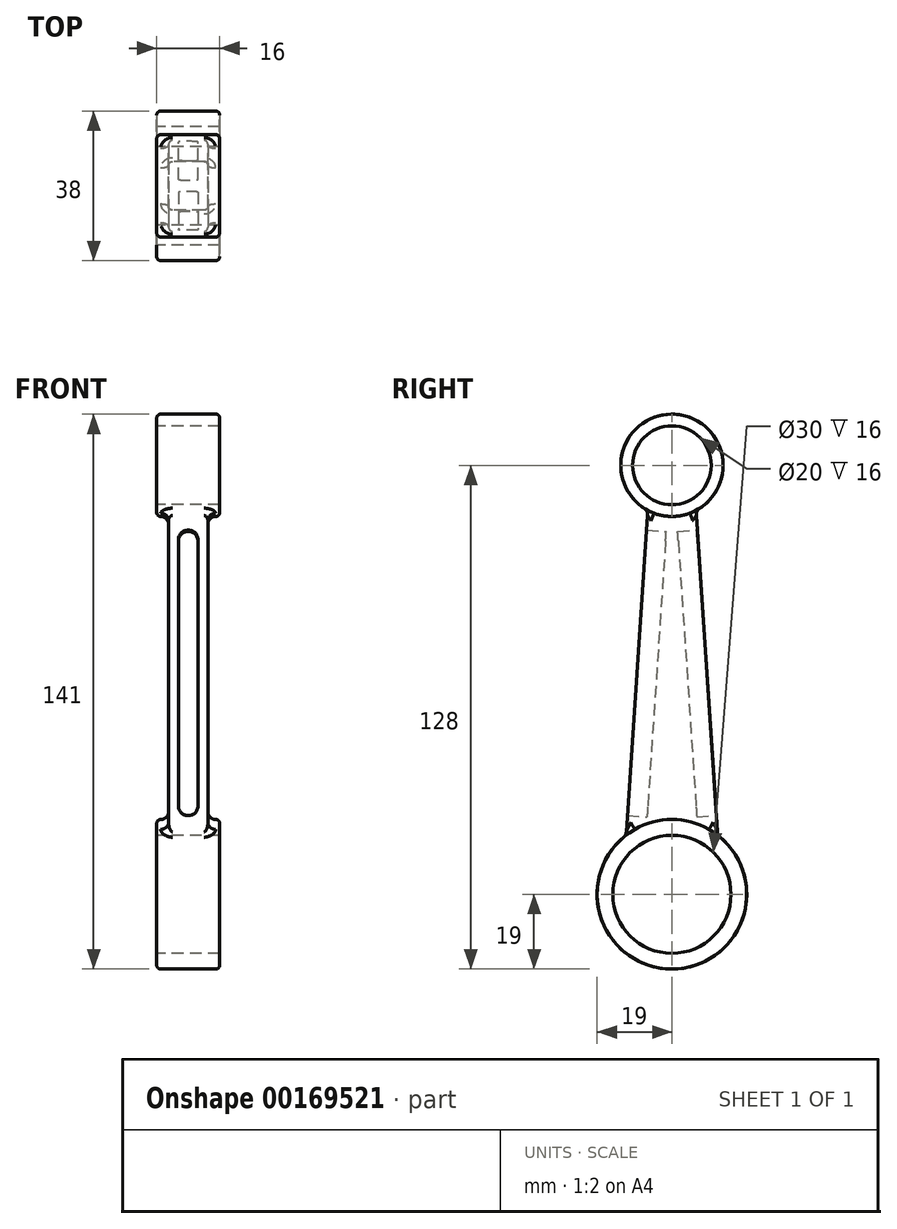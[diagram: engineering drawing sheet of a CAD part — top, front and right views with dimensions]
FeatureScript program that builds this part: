
annotation { "Feature Type Name" : "Feature", "Feature Type Description" : "" }
export const myFeature = defineFeature(function(context is Context, id is Id, definition is map)
    precondition{}
    {
        {
            assignVariable(context, id + "F0", {"name" : "BearingWidth", "anyValue" : 16});
        }
        {
            assignVariable(context, id + "F1", {"name" : "RodWidth", "anyValue" : 10});
        }
        {
            var Q0;
            Q0=qCreatedBy(makeId("Right.planeOp"),FACE);
            var sketch = newSketch(context, id + "F2", { "sketchPlane" : qUnion([Q0])});
            skCircle(sketch, "E0", {"center": v(0, 0) * mm, "radius": 19 * mm});
            skLineSegment(sketch, "E1", {"start": v(0, -34.78) * mm, "end": v(0, 151.53) * mm, "construction": true});
            skCircle(sketch, "E2", {"center": v(0, 109) * mm, "radius": 13 * mm});
            skCircle(sketch, "E3", {"center": v(0, 0) * mm, "radius": 15 * mm});
            skCircle(sketch, "E4", {"center": v(0, 109) * mm, "radius": 10 * mm});
            skSolve(sketch);
        }
        {
            var Q0;
            Q0 = qSketchRegion(id + "F2", true);
            extrude(context, id + "F3", {"entities" : qUnion([Q0]), "endBound" : BoundingType.SYMMETRIC, "depth" : (getVariable(context, 'BearingWidth')) * mm});
        }
        {
            var Q0;
            Q0=qCreatedBy(makeId("Right.planeOp"),FACE);
            var sketch = newSketch(context, id + "F4", { "sketchPlane" : qUnion([Q0])});
            skLineSegment(sketch, "E5", {"start": v(0, 136.56) * mm, "end": v(0, -23.65) * mm, "construction": true});
            skLineSegment(sketch, "E6", {"start": v(6, 99) * mm, "end": v(-6, 99) * mm});
            skCircle(sketch, "E7.0", {"center": v(0, 109) * mm, "radius": 10 * mm});
            skPoint(sketch, "E8", {"position": v(0, 99) * mm});
            skCircle(sketch, "E9.0", {"center": v(0, 0) * mm, "radius": 15 * mm});
            skPoint(sketch, "E10", {"position": v(0, 16.05) * mm});
            skLineSegment(sketch, "E11", {"start": v(0, 16.05) * mm, "end": v(-12, 9.7) * mm});
            skLineSegment(sketch, "E12", {"start": v(0, 16.05) * mm, "end": v(12, 9.7) * mm});
            skLineSegment(sketch, "E13", {"start": v(-6, 99) * mm, "end": v(-12, 9.7) * mm});
            skLineSegment(sketch, "E14", {"start": v(6, 99) * mm, "end": v(12, 9.7) * mm});
            skSolve(sketch);
        }
        {
            var Q0;
            Q0=makeQuery(id+"F4.imprint","IMPRINT",FACE,{"disambiguationData":[TD([[makeQuery(id+"F4.imprint","IMPRINT",EDGE,{"derivedFrom":sQuery(id+"F4.wireOp",EDGE,"E11")}),-1.0]])]});
            extrude(context, id + "F5", {"entities" : qUnion([Q0]), "operationType" : NewBodyOperationType.ADD, "endBound" : BoundingType.SYMMETRIC, "depth" : (getVariable(context, 'RodWidth')) * mm});
        }
        {
            var Q0;
            Q0=makeQuery(id+"F5.opExtrude","CAP_EDGE",EDGE,{"disambiguationData":[OSD([sQuery(id+"F4.wireOp",EDGE,"E13")])],"isStart":false});
            var Q1;
            Q1=makeQuery(id+"F3.opExtrude","CAP_EDGE",EDGE,{"disambiguationData":[OSD([sQuery(id+"F2.wireOp",EDGE,"E0")])],"isStart":false});
            var Q2;
            Q2=makeQuery(id+"F5.opExtrude","CAP_EDGE",EDGE,{"disambiguationData":[OSD([sQuery(id+"F4.wireOp",EDGE,"E14")])],"isStart":false});
            var Q3;
            Q3=makeQuery(id+"F3.opExtrude","CAP_EDGE",EDGE,{"disambiguationData":[OSD([sQuery(id+"F2.wireOp",EDGE,"E2")])],"isStart":false});
            var Q4;
            Q4=makeQuery(id+"F3.opExtrude","CAP_EDGE",EDGE,{"disambiguationData":[OSD([sQuery(id+"F2.wireOp",EDGE,"E0")])],"isStart":true});
            var Q5;
            Q5=makeQuery(id+"F5.opExtrude","CAP_EDGE",EDGE,{"disambiguationData":[OSD([sQuery(id+"F4.wireOp",EDGE,"E14")])],"isStart":true});
            var Q6;
            Q6=makeQuery(id+"F5.opExtrude","CAP_EDGE",EDGE,{"disambiguationData":[OSD([sQuery(id+"F4.wireOp",EDGE,"E13")])],"isStart":true});
            var Q7;
            Q7=makeQuery(id+"F3.opExtrude","CAP_EDGE",EDGE,{"disambiguationData":[OSD([sQuery(id+"F2.wireOp",EDGE,"E2")])],"isStart":true});
            fillet(context, id + "F6", {"entities" : qUnion([Q0, Q1, Q2, Q3, Q4, Q5, Q6, Q7]), "radius" : 1 * mm, "tangentPropagation" : true, "allowEdgeOverflow" : false});
        }
        {
            var Q0;
            Q0=makeQuery(id+"F5.opExtrude","SWEPT_FACE",FACE,{"disambiguationData":[OSD([sQuery(id+"F4.wireOp",EDGE,"E14")])]});
            var sketch = newSketch(context, id + "F7", { "sketchPlane" : qUnion([Q0])});
            skLineSegment(sketch, "E15", {"start": v(0, -3.9) * mm, "end": v(0, 157.82) * mm, "construction": true});
            skLineSegment(sketch, "E16.bottom", {"start": v(-2.5, 91.9) * mm, "end": v(2.5, 91.9) * mm});
            skLineSegment(sketch, "E16.top", {"start": v(-2.5, 19.2) * mm, "end": v(2.5, 19.2) * mm});
            skLineSegment(sketch, "E16.left", {"start": v(-2.5, 91.9) * mm, "end": v(-2.5, 19.2) * mm});
            skLineSegment(sketch, "E16.right", {"start": v(2.5, 91.9) * mm, "end": v(2.5, 19.2) * mm});
            skSolve(sketch);
        }
        {
            var Q0;
            Q0 = qSketchRegion(id + "F7", true);
            extrude(context, id + "F8", {"entities" : qUnion([Q0]), "operationType" : NewBodyOperationType.REMOVE, "oppositeDirection" : true, "depth" : 5 * mm});
        }
        {
            var Q0;
            Q0=makeQuery(id+"F8.boolean.opBoolean","COPY",EDGE,{"derivedFrom":makeQuery(id+"F8.opExtrude","SWEPT_EDGE",EDGE,{"disambiguationData":[OSD([sQuery(id+"F7.wireOp",EDGE,"E16.bottom"),sQuery(id+"F7.wireOp",EDGE,"E16.left")])]})});
            var Q1;
            Q1=makeQuery(id+"F8.boolean.opBoolean","COPY",EDGE,{"derivedFrom":makeQuery(id+"F8.opExtrude","SWEPT_EDGE",EDGE,{"disambiguationData":[OSD([sQuery(id+"F7.wireOp",EDGE,"E16.bottom"),sQuery(id+"F7.wireOp",EDGE,"E16.right")])]})});
            var Q2;
            Q2=makeQuery(id+"F8.boolean.opBoolean","COPY",EDGE,{"derivedFrom":makeQuery(id+"F8.opExtrude","SWEPT_EDGE",EDGE,{"disambiguationData":[OSD([sQuery(id+"F7.wireOp",EDGE,"E16.top"),sQuery(id+"F7.wireOp",EDGE,"E16.right")])]})});
            var Q3;
            Q3=makeQuery(id+"F8.boolean.opBoolean","COPY",EDGE,{"derivedFrom":makeQuery(id+"F8.opExtrude","SWEPT_EDGE",EDGE,{"disambiguationData":[OSD([sQuery(id+"F7.wireOp",EDGE,"E16.top"),sQuery(id+"F7.wireOp",EDGE,"E16.left")])]})});
            fillet(context, id + "F9", {"entities" : qUnion([Q0, Q1, Q2, Q3]), "radius" : 2.5 * mm, "tangentPropagation" : true, "allowEdgeOverflow" : false});
        }
        {
            var Q0;
            Q0=makeQuery(id+"F5.opExtrude","SWEPT_FACE",FACE,{"disambiguationData":[OSD([sQuery(id+"F4.wireOp",EDGE,"E13")])]});
            var sketch = newSketch(context, id + "F10", { "sketchPlane" : qUnion([Q0])});
            skLineSegment(sketch, "E17", {"start": v(0, 0) * mm, "end": v(0, 109.28) * mm, "construction": true});
            skPoint(sketch, "E17.endSnap0", {"position": v(0, 96.9) * mm});
            skLineSegment(sketch, "E18.bottom", {"start": v(-2.5, 91.9) * mm, "end": v(2.5, 91.9) * mm});
            skLineSegment(sketch, "E18.top", {"start": v(-2.5, 19.2) * mm, "end": v(2.5, 19.2) * mm});
            skLineSegment(sketch, "E18.left", {"start": v(-2.5, 91.9) * mm, "end": v(-2.5, 19.2) * mm});
            skLineSegment(sketch, "E18.right", {"start": v(2.5, 91.9) * mm, "end": v(2.5, 19.2) * mm});
            skSolve(sketch);
        }
        {
            var Q0;
            Q0 = qSketchRegion(id + "F10", true);
            extrude(context, id + "F11", {"entities" : qUnion([Q0]), "operationType" : NewBodyOperationType.REMOVE, "oppositeDirection" : true, "depth" : 5 * mm});
        }
        {
            var Q0;
            Q0=makeQuery(id+"F11.boolean.opBoolean","COPY",EDGE,{"derivedFrom":makeQuery(id+"F11.opExtrude","SWEPT_EDGE",EDGE,{"disambiguationData":[OSD([sQuery(id+"F10.wireOp",EDGE,"E18.bottom"),sQuery(id+"F10.wireOp",EDGE,"E18.right")])]})});
            var Q1;
            Q1=makeQuery(id+"F11.boolean.opBoolean","COPY",EDGE,{"derivedFrom":makeQuery(id+"F11.opExtrude","SWEPT_EDGE",EDGE,{"disambiguationData":[OSD([sQuery(id+"F10.wireOp",EDGE,"E18.bottom"),sQuery(id+"F10.wireOp",EDGE,"E18.left")])]})});
            var Q2;
            Q2=makeQuery(id+"F11.boolean.opBoolean","COPY",EDGE,{"derivedFrom":makeQuery(id+"F11.opExtrude","SWEPT_EDGE",EDGE,{"disambiguationData":[OSD([sQuery(id+"F10.wireOp",EDGE,"E18.top"),sQuery(id+"F10.wireOp",EDGE,"E18.left")])]})});
            var Q3;
            Q3=makeQuery(id+"F11.boolean.opBoolean","COPY",EDGE,{"derivedFrom":makeQuery(id+"F11.opExtrude","SWEPT_EDGE",EDGE,{"disambiguationData":[OSD([sQuery(id+"F10.wireOp",EDGE,"E18.top"),sQuery(id+"F10.wireOp",EDGE,"E18.right")])]})});
            fillet(context, id + "F12", {"entities" : qUnion([Q0, Q1, Q2, Q3]), "radius" : 2.5 * mm, "tangentPropagation" : true, "allowEdgeOverflow" : false});
        }
        {
            var Q0;
            Q0=makeQuery(id+"F5.boolean.opBoolean","INTERSECT",EDGE,{"derivedFrom":[makeQuery(id+"F3.opExtrude","SWEPT_FACE",FACE,{"disambiguationData":[OSD([sQuery(id+"F2.wireOp",EDGE,"E0")])]}),makeQuery(id+"F5.opExtrude","SWEPT_FACE",FACE,{"disambiguationData":[OSD([sQuery(id+"F4.wireOp",EDGE,"E13")])]})]});
            var Q1;
            Q1=makeQuery(id+"F5.boolean.opBoolean","INTERSECT",EDGE,{"derivedFrom":[makeQuery(id+"F3.opExtrude","SWEPT_FACE",FACE,{"disambiguationData":[OSD([sQuery(id+"F2.wireOp",EDGE,"E2")])]}),makeQuery(id+"F5.opExtrude","SWEPT_FACE",FACE,{"disambiguationData":[OSD([sQuery(id+"F4.wireOp",EDGE,"E13")])]})]});
            fillet(context, id + "F13", {"entities" : qUnion([Q0, Q1]), "radius" : 2 * mm, "tangentPropagation" : true, "allowEdgeOverflow" : false});
        }
    });
